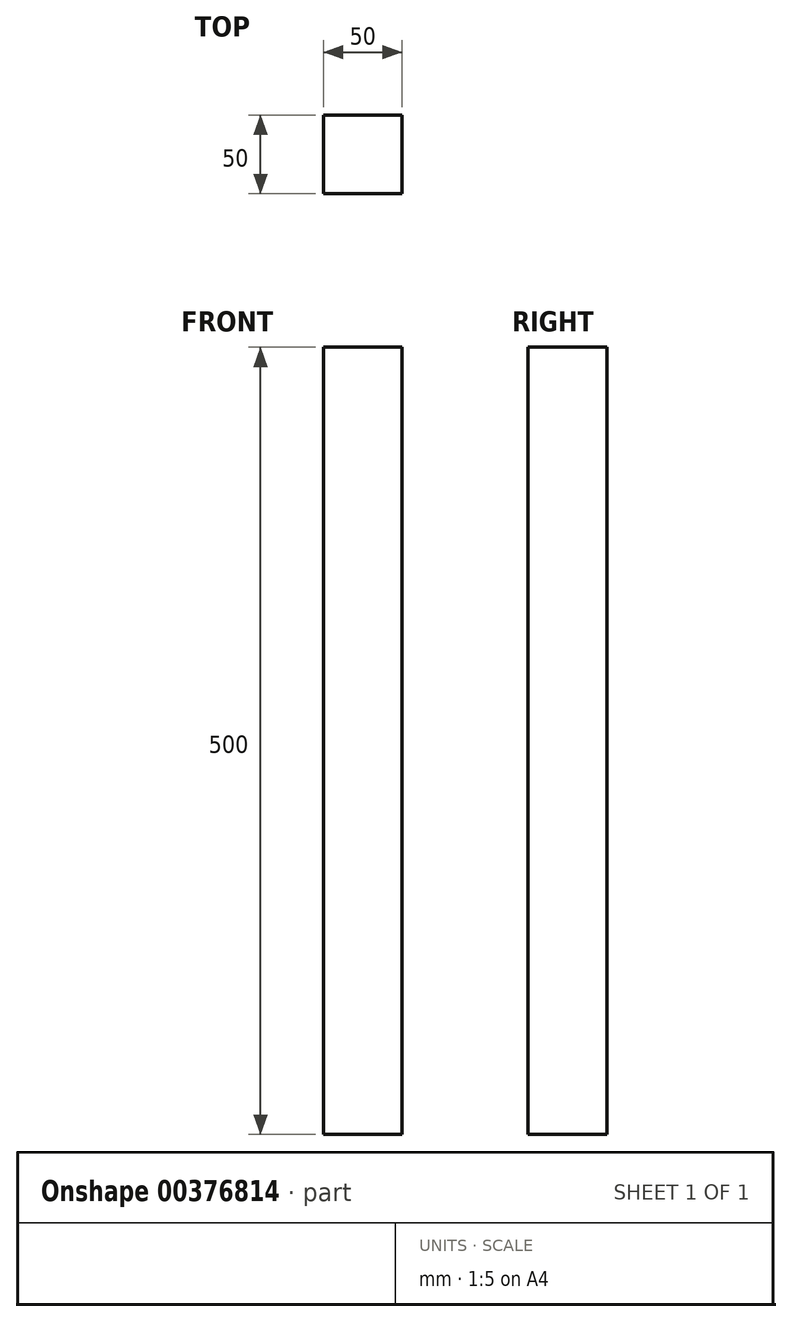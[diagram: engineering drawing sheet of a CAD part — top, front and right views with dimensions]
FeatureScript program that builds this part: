
annotation { "Feature Type Name" : "Feature", "Feature Type Description" : "" }
export const myFeature = defineFeature(function(context is Context, id is Id, definition is map)
    precondition{}
    {
        {
            var Q0;
            Q0=qCreatedBy(makeId("Top.planeOp"),FACE);
            var sketch = newSketch(context, id + "F0", { "sketchPlane" : qUnion([Q0])});
            skLineSegment(sketch, "E0.bottom", {"start": v(-48.54, -22.7) * mm, "end": v(-98.54, -22.7) * mm});
            skLineSegment(sketch, "E0.top", {"start": v(-48.54, 27.3) * mm, "end": v(-98.54, 27.3) * mm});
            skLineSegment(sketch, "E0.left", {"start": v(-48.54, -22.7) * mm, "end": v(-48.54, 27.3) * mm});
            skLineSegment(sketch, "E0.right", {"start": v(-98.54, -22.7) * mm, "end": v(-98.54, 27.3) * mm});
            skPoint(sketch, "E0.middle", {"position": v(-73.54, 2.3) * mm});
            skSolve(sketch);
        }
        {
            var Q0;
            Q0=qSketchRegion(id+"F0",true);
            extrude(context, id + "F1", {"entities" : qUnion([Q0]), "depth" : 15 * mm});
        }
        {
            var Q0;
            Q0=qSketchRegion(id+"F0",true);
            extrude(context, id + "F2", {"entities" : qUnion([Q0]), "operationType" : NewBodyOperationType.ADD, "depth" : 500 * mm});
        }
    });
